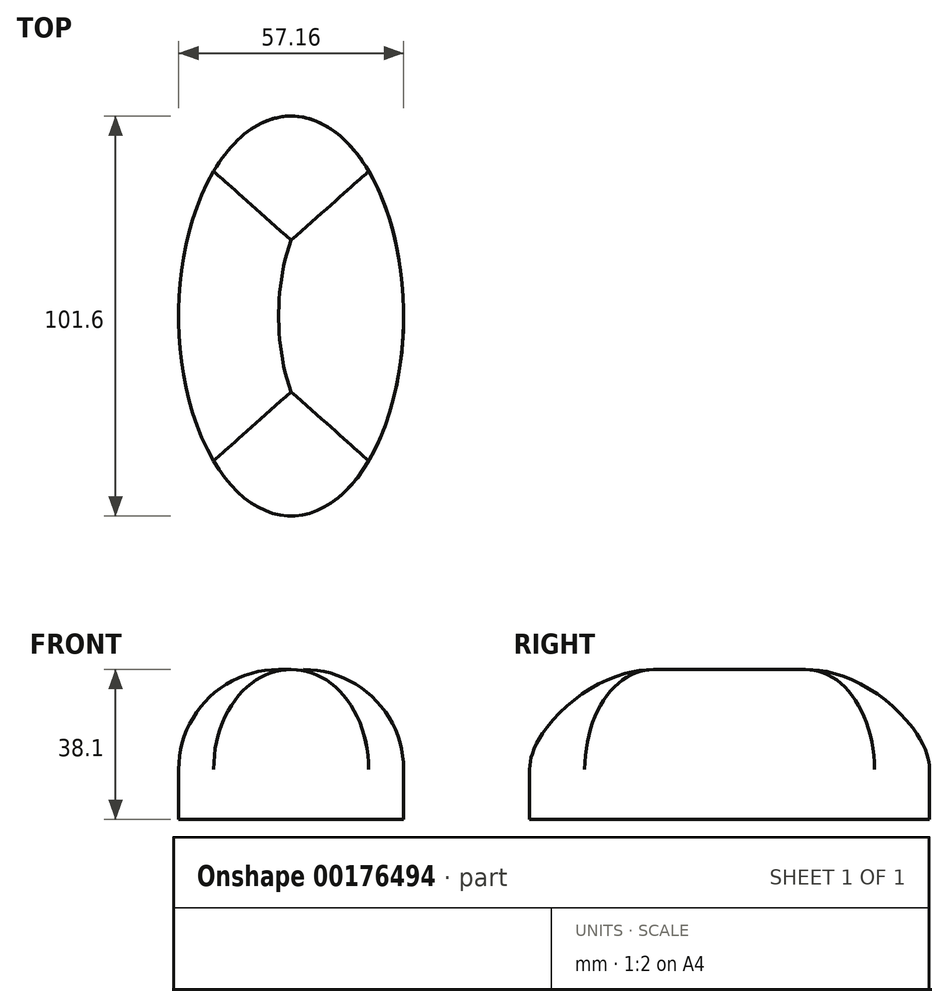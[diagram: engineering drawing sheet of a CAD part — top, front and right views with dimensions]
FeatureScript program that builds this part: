
annotation { "Feature Type Name" : "Feature", "Feature Type Description" : "" }
export const myFeature = defineFeature(function(context is Context, id is Id, definition is map)
    precondition{}
    {
        {
            var Q0;
            Q0=qCreatedBy(makeId("Top.planeOp"),FACE);
            var sketch = newSketch(context, id + "F0", { "sketchPlane" : qUnion([Q0])});
            skEllipse(sketch, "E0", {"center": v(0, 0) * mm, "majorRadius": 50.8 * mm, "minorRadius": 28.58 * mm, "majorAxis": v(0, 1)});
            skSolve(sketch);
        }
        {
            var Q0;
            Q0 = qSketchRegion(id + "F0", true);
            extrude(context, id + "F1", {"entities" : qUnion([Q0]), "depth" : 38.1 * mm});
        }
        {
            var Q0;
            Q0=makeQuery(id+"F1.opExtrude","CAP_EDGE",EDGE,{"disambiguationData":[OSD([sQuery(id+"F0.wireOp",EDGE,"E0")])],"isStart":false});
            fillet(context, id + "F2", {"entities" : qUnion([Q0]), "radius" : 25.4 * mm, "tangentPropagation" : true, "allowEdgeOverflow" : false});
        }
    });
